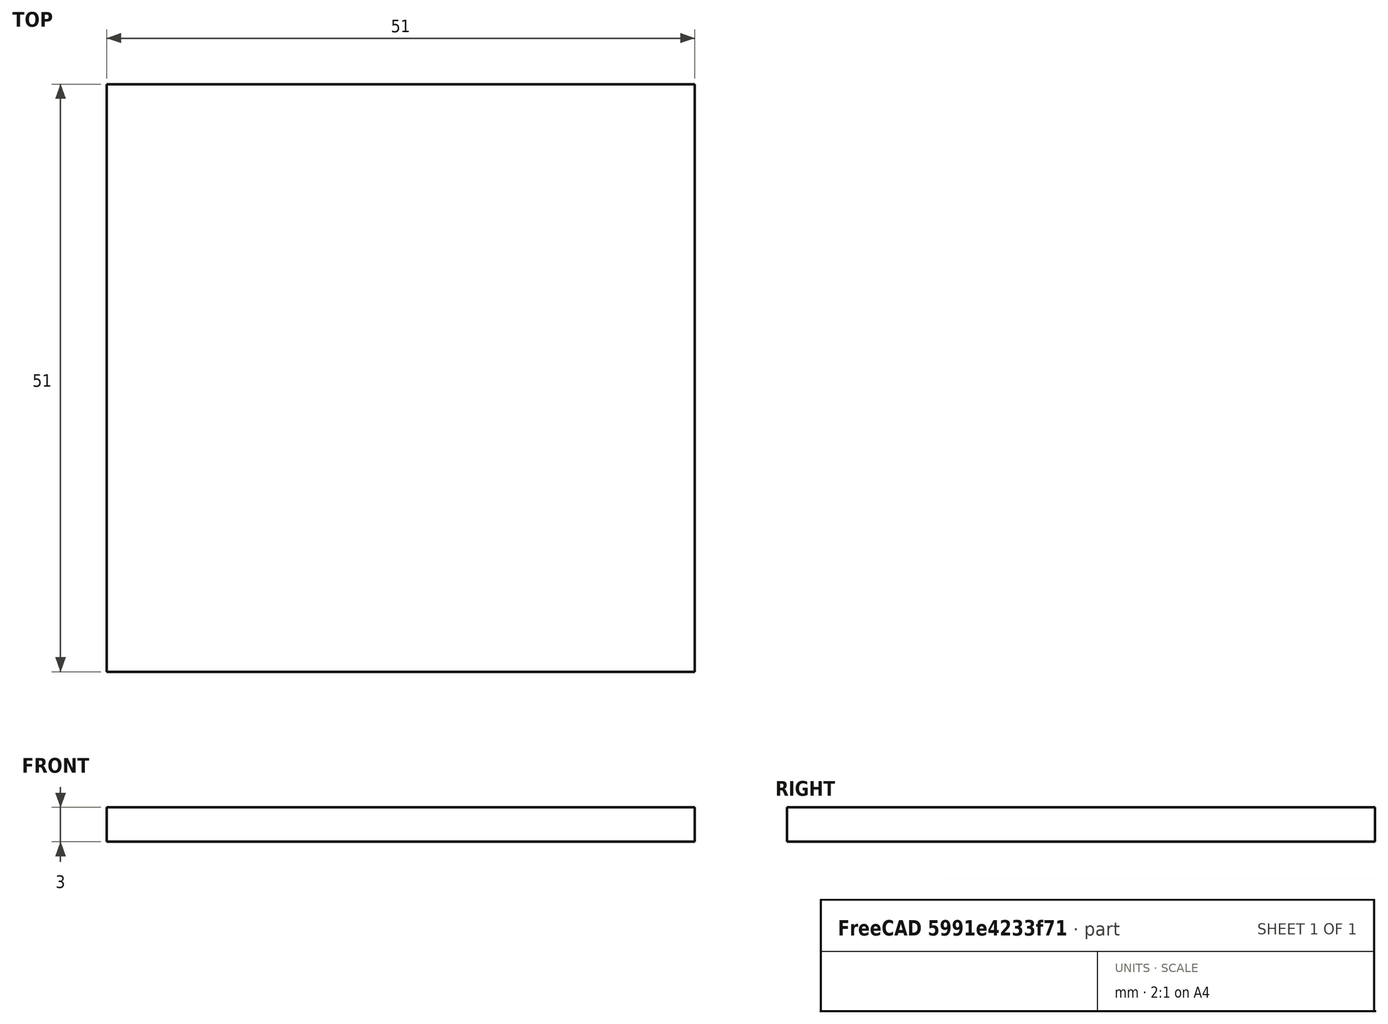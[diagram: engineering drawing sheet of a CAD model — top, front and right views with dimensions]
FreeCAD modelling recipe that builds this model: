
FCSTD DOCUMENT  (FreeCAD 0.18.4R)
Label: bg3_example
License: All rights reserved
LicenseURL: http://en.wikipedia.org/wiki/All_rights_reserved
objects: Sketcher::SketchObject×1, PartDesign::Pad×1, PartDesign::Body×1
note: 4 computed .brp shape members not serialized (recipe doc carries the construction recipe); baked Part::Feature solids carry a one-line shape summary decoded from their .brp

FEATURE [Sketcher::SketchObject] Sketch
  MapMode = 5
  Support = -> [XY_Plane]
  sketch-geometry (4):
    g0: LineSegment StartX=0 StartY=0 StartZ=0 EndX=51 EndY=0 EndZ=0
    g1: LineSegment StartX=51 StartY=0 StartZ=0 EndX=51 EndY=51 EndZ=0
    g2: LineSegment StartX=51 StartY=51 StartZ=0 EndX=0 EndY=51 EndZ=0
    g3: LineSegment StartX=0 StartY=51 StartZ=0 EndX=0 EndY=0 EndZ=0
  constraints (11):
    c: Coincident(g0,g1)
    c: Coincident(g1,g2)
    c: Coincident(g2,g3)
    c: Coincident(g3,g0)
    c: Horizontal(g0)
    c: Horizontal(g2)
    c: Vertical(g1)
    c: Vertical(g3)
    c: Coincident(g0,g-1)
    c: Equal(g1,g2)
    c: DistanceY(g3,g3) = 51
FEATURE [PartDesign::Pad] Pad
  Length = 3
  Length2 = 100
  Profile = -> Sketch
  Type = 0
FEATURE [PartDesign::Body] Body
  Group = -> [Sketch,Pad]
  Origin = -> Origin
  Tip = -> Pad
